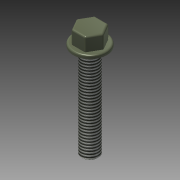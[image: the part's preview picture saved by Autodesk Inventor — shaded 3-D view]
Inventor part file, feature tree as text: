
AUTODESK INVENTOR PART (.ipt)
format: ipt  version: 2015 (Build 190159000, 159)  size: 130,048 bytes
history: native  units: mm
features: extrude x3, sketch x3, fillet x1, thread x1, chamfer x1
ambient origin geometry x8: Origin, YZ Plane, XZ Plane, XY Plane, X Axis, Y Axis, Z Axis, Center Point
bodies: 实体1 (feature_tree)
feature tree (9):
  extrude  "拉伸1"  Depth=1.0mm TaperAngle=0.0deg
  extrude  "拉伸2"  Depth=4.0mm
  fillet  "圆角1"  Radius=4.0mm
  extrude  "拉伸3"  Depth=5.0mm
  thread  "螺纹1"  [1 undecoded]
  chamfer  "倒角1"  Distance=10.0mm
  sketch  "草图1"  dims[d0=10.0mm d1=1.0mm d2=0.0mm]
  sketch  "草图2"  dims[d3=1.405329mm d4=3.5mm d5=4.0mm d6=0.0mm]
  sketch  "草图3"  dims[d7=0.5mm d8=5.0mm d9=28.0mm d10=0.0mm d11=10.0mm d12=0.0mm d13=0.25mm d14=2.0mm d15=45.0deg]
note: 1 required parameter value undecoded (feature->parameter linkage not recoverable at this tier; creation-order binding heuristic only, values carry confidence <= 0.55)
